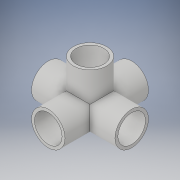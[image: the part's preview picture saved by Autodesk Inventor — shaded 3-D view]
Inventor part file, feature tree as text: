
AUTODESK INVENTOR PART (.ipt)
format: ipt  version: 2018 (Build 220112000, 112)  size: 204,288 bytes
history: native  units: in
note: dims shown in document units (in); Inventor stores cm internally (conversion verified against a paired STEP export)
features: sketch x15, extrude x11, plane x2
ambient origin geometry x8: Origin, YZ Plane, XZ Plane, XY Plane, X Axis, Y Axis, Z Axis, Center Point
bodies: Solid1 (feature_tree)
feature tree (28):
  extrude  "Extrusion1"  Depth=4.0in TaperAngle=0.0deg
  sketch  "Sketch2"  dims[d3=4.0in d4=0.0in d5=1.321in]
  sketch  "Sketch3"  dims[d6=1.321in d7=1.321in]
  sketch  "Sketch11"  dims[d32=2.0in d33=0.0in]
  sketch  "Sketch12"
  plane  "Work Plane1"
  plane  "Work Plane2"
  extrude  "Extrusion2"  Depth=1.321in
  sketch  "Sketch13"
  extrude  "Extrusion9"  Depth=1.321in
  sketch  "Sketch5"  dims[d11=1.25in d12=0.0in d13=1.25in d14=0.0in]
  sketch  "Sketch6"  dims[d15=1.25in d16=0.0in d17=1.0in]
  sketch  "Sketch7"  dims[d18=1.0in d19=4.0in d20=0.0in]
  sketch  "Sketch8"  dims[d21=4.0in d22=0.0in d23=1.605in]
  extrude  "Extrusion3"  Depth=1.25in TaperAngle=0.0deg
  extrude  "Extrusion4"  Depth=1.25in TaperAngle=0.0deg
  extrude  "Extrusion5"  Depth=1.0in
  extrude  "Extrusion6"  Depth=4.0in TaperAngle=0.0deg
  sketch  "Sketch9"  dims[d24=1.1975in d25=0.8025in d26=0.0in d27=0.0in d28=1.321in]
  extrude  "Extrusion7"  Depth=1.605in
  extrude  "Extrusion8"  Depth=1.321in
  extrude  "Extrusion10"  Depth=1.0in
  extrude  "Extrusion11"  [1 undecoded]
  sketch  "Sketch1"  dims[d0=1.605in d1=4.0in d2=0.0in]
  sketch  "Sketch4"  dims[d8=1.321in d9=1.25in d10=0.0in]
  sketch  "Sketch10"  dims[d29=1.25in d30=0.0in d31=1.0in]
  sketch  "Sketch14"
  sketch  "Sketch15"
note: 1 required parameter value undecoded (feature->parameter linkage not recoverable at this tier; creation-order binding heuristic only, values carry confidence <= 0.55)
